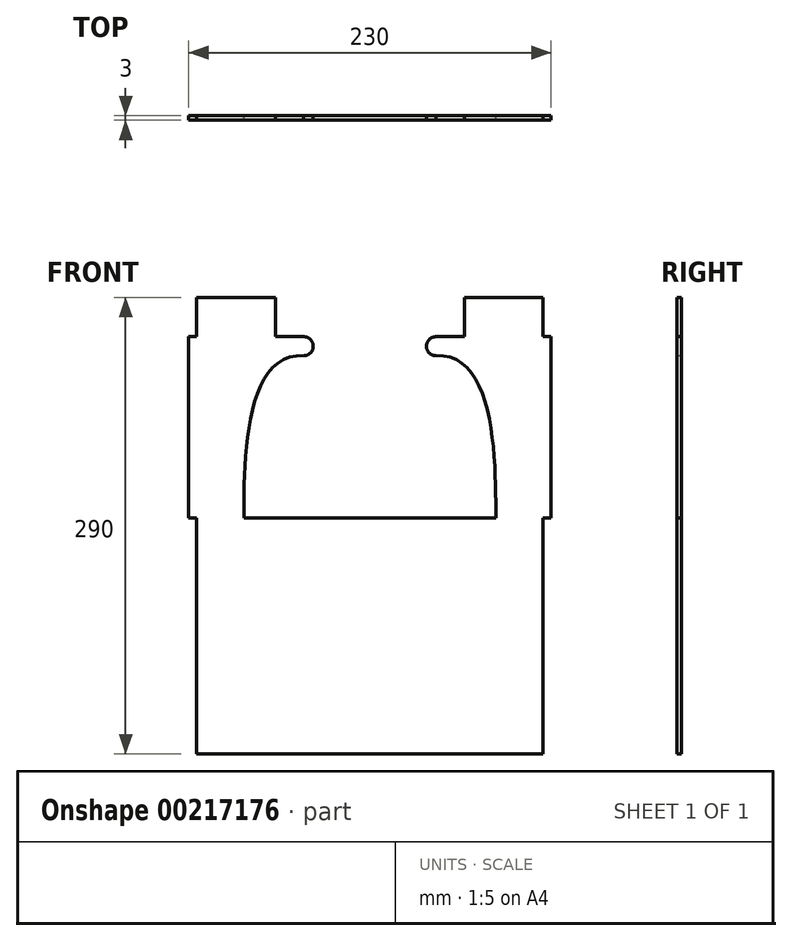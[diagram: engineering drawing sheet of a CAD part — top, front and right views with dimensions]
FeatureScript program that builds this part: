
annotation { "Feature Type Name" : "Feature", "Feature Type Description" : "" }
export const myFeature = defineFeature(function(context is Context, id is Id, definition is map)
    precondition{}
    {
        {
            var Q0;
            Q0=qCreatedBy(makeId("Front.planeOp"),FACE);
            var sketch = newSketch(context, id + "F0", { "sketchPlane" : qUnion([Q0])});
            skLineSegment(sketch, "E0.bottom", {"start": v(-110, 75) * mm, "end": v(110, 75) * mm});
            skLineSegment(sketch, "E0.top", {"start": v(-110, -75) * mm, "end": v(110, -75) * mm});
            skLineSegment(sketch, "E0.left", {"start": v(-110, 75) * mm, "end": v(-110, -75) * mm});
            skLineSegment(sketch, "E0.right", {"start": v(110, 75) * mm, "end": v(110, -75) * mm});
            skPoint(sketch, "E0.middle", {"position": v(0, 0) * mm});
            skPoint(sketch, "E1", {"position": v(-80, 75) * mm});
            skPoint(sketch, "E2", {"position": v(80, 75) * mm});
            skLineSegment(sketch, "E3", {"start": v(-80, 75) * mm, "end": v(-80, -75) * mm});
            skLineSegment(sketch, "E4", {"start": v(80, 75) * mm, "end": v(80, -75) * mm});
            skLineSegment(sketch, "E5.bottom", {"start": v(-110, 75) * mm, "end": v(-80, 75) * mm});
            skLineSegment(sketch, "E5.top", {"start": v(-110, 190) * mm, "end": v(-80, 190) * mm});
            skLineSegment(sketch, "E5.left", {"start": v(-110, 75) * mm, "end": v(-110, 190) * mm});
            skLineSegment(sketch, "E5.right", {"start": v(-80, 75) * mm, "end": v(-80, 190) * mm});
            skLineSegment(sketch, "E6", {"start": v(-80, 190) * mm, "end": v(-42, 190) * mm});
            skArc(sketch, "E7", {"start": v(-42, 190) * mm, "mid": v(-35.94, 184.06) * mm, "end": v(-41.87, 178) * mm});
            skFitSpline(sketch, "E8", {"points": [v(-41.87, 178) * mm, v(-80, 75) * mm], "startDerivative": vector(-114.39, 6.08) * mm, "endDerivative": vector(0, -107.82) * mm});
            skLineSegment(sketch, "E9", {"start": v(0, 0) * mm, "end": v(0, 29.27) * mm});
            skLineSegment(sketch, "E10.MirrorCS", {"start": v(80, 75) * mm, "end": v(80, 190) * mm});
            skLineSegment(sketch, "E11.MirrorCS", {"start": v(110, 75) * mm, "end": v(110, 190) * mm});
            skLineSegment(sketch, "E12.MirrorCS", {"start": v(110, 190) * mm, "end": v(80, 190) * mm});
            skLineSegment(sketch, "E13.MirrorCS", {"start": v(80, 190) * mm, "end": v(42, 190) * mm});
            skArc(sketch, "E14.MirrorCS", {"start": v(42, 190) * mm, "mid": v(35.94, 184.06) * mm, "end": v(41.87, 178) * mm});
            skFitSpline(sketch, "E15.MirrorCS", {"points": [v(41.87, 178) * mm, v(80, 75) * mm], "startDerivative": vector(114.39, 6.08) * mm, "endDerivative": vector(0, -107.82) * mm});
            skLineSegment(sketch, "E16.bottom", {"start": v(-110, 190) * mm, "end": v(-60, 190) * mm});
            skLineSegment(sketch, "E16.top", {"start": v(-110, 215) * mm, "end": v(-60, 215) * mm});
            skLineSegment(sketch, "E16.left", {"start": v(-110, 190) * mm, "end": v(-110, 215) * mm});
            skLineSegment(sketch, "E16.right", {"start": v(-60, 190) * mm, "end": v(-60, 215) * mm});
            skLineSegment(sketch, "E17.bottom", {"start": v(-110, 75) * mm, "end": v(-115, 75) * mm});
            skLineSegment(sketch, "E17.top", {"start": v(-110, 190) * mm, "end": v(-110, 190) * mm});
            skLineSegment(sketch, "E18", {"start": v(-115, 75) * mm, "end": v(-115, 190) * mm});
            skLineSegment(sketch, "E19", {"start": v(-115, 190) * mm, "end": v(-110, 190) * mm});
            skLineSegment(sketch, "E20.MirrorCS", {"start": v(115, 75) * mm, "end": v(115, 190) * mm});
            skLineSegment(sketch, "E21.MirrorCS", {"start": v(115, 190) * mm, "end": v(110, 190) * mm});
            skLineSegment(sketch, "E22.MirrorCS", {"start": v(110, 75) * mm, "end": v(115, 75) * mm});
            skLineSegment(sketch, "E23.MirrorCS", {"start": v(110, 215) * mm, "end": v(60, 215) * mm});
            skLineSegment(sketch, "E24.MirrorCS", {"start": v(60, 190) * mm, "end": v(60, 215) * mm});
            skLineSegment(sketch, "E25.MirrorCS", {"start": v(110, 190) * mm, "end": v(110, 215) * mm});
            skLineSegment(sketch, "E26", {"start": v(-42, 190) * mm, "end": v(-41.87, 178) * mm});
            skPoint(sketch, "E27.endSnap0", {"position": v(-35.94, 184.06) * mm});
            skSolve(sketch);
        }
        {
            var Q0;
            Q0 = qSketchRegion(id + "F0", true);
            extrude(context, id + "F1", {"entities" : qUnion([Q0]), "depth" : 3 * mm});
        }
    });
